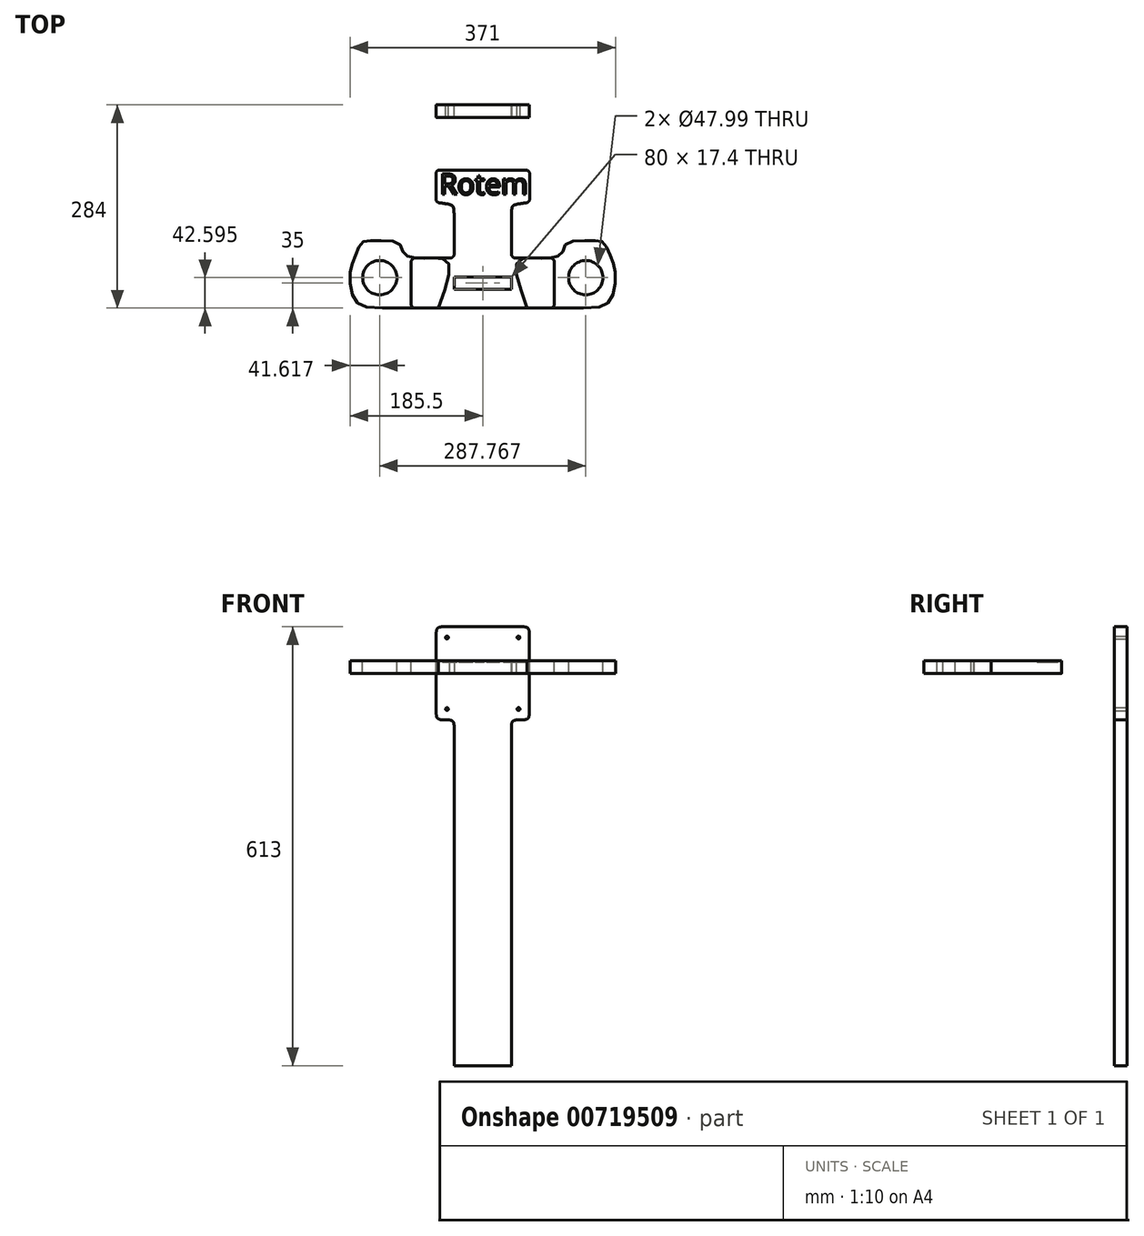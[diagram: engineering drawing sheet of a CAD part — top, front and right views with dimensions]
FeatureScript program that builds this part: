
annotation { "Feature Type Name" : "Feature", "Feature Type Description" : "" }
export const myFeature = defineFeature(function(context is Context, id is Id, definition is map)
    precondition{}
    {
        {
            var Q0;
            Q0=qCreatedBy(makeId("Front.planeOp"),FACE);
            var sketch = newSketch(context, id + "F0", { "sketchPlane" : qUnion([Q0])});
            skLineSegment(sketch, "E0.bottom", {"start": v(-65, 65) * mm, "end": v(65, 65) * mm});
            skLineSegment(sketch, "E0.top", {"start": v(-65, -65) * mm, "end": v(-40, -65) * mm});
            skLineSegment(sketch, "E0.left", {"start": v(-65, 65) * mm, "end": v(-65, -65) * mm});
            skLineSegment(sketch, "E0.right", {"start": v(65, 65) * mm, "end": v(65, -65) * mm});
            skPoint(sketch, "E0.middle", {"position": v(0, 0) * mm});
            skLineSegment(sketch, "E1", {"start": v(-65, 65) * mm, "end": v(65, -65) * mm, "construction": true});
            skLineSegment(sketch, "E2.bottom", {"start": v(-50, 50) * mm, "end": v(50, 50) * mm, "construction": true});
            skLineSegment(sketch, "E2.top", {"start": v(-50, -50) * mm, "end": v(50, -50) * mm, "construction": true});
            skLineSegment(sketch, "E2.left", {"start": v(-50, 50) * mm, "end": v(-50, -50) * mm, "construction": true});
            skLineSegment(sketch, "E2.right", {"start": v(50, 50) * mm, "end": v(50, -50) * mm, "construction": true});
            skCircle(sketch, "E3", {"center": v(-50, 50) * mm, "radius": 2 * mm});
            skCircle(sketch, "E4", {"center": v(50, 50) * mm, "radius": 2 * mm});
            skCircle(sketch, "E5", {"center": v(50, -50) * mm, "radius": 2 * mm});
            skCircle(sketch, "E6", {"center": v(-50, -50) * mm, "radius": 2 * mm});
            skLineSegment(sketch, "E7", {"start": v(-40, -548) * mm, "end": v(40, -548) * mm});
            skLineSegment(sketch, "E8", {"start": v(-40, -548) * mm, "end": v(-40, -65) * mm});
            skLineSegment(sketch, "E9", {"start": v(40, -548) * mm, "end": v(40, -65) * mm});
            skLineSegment(sketch, "E10.trimOffspring", {"start": v(40, -65) * mm, "end": v(65, -65) * mm});
            skSolve(sketch);
        }
        {
            var Q0;
            Q0=makeQuery(id+"F0.imprint","IMPRINT",FACE,{"disambiguationData":[TD([[makeQuery(id+"F0.imprint","IMPRINT",EDGE,{"derivedFrom":sQuery(id+"F0.wireOp",EDGE,"E0.bottom")}),-1.0]])]});
            var Q1;
            Q1=sQuery(id+"F0.wireOp",EDGE,"E8");
            var Q2;
            Q2=sQuery(id+"F0.wireOp",EDGE,"E0.top");
            var Q3;
            Q3=sQuery(id+"F0.wireOp",EDGE,"E0.left");
            var Q4;
            Q4=sQuery(id+"F0.wireOp",EDGE,"E0.bottom");
            var Q5;
            Q5=sQuery(id+"F0.wireOp",EDGE,"E0.right");
            var Q6;
            Q6=sQuery(id+"F0.wireOp",EDGE,"E10.trimOffspring");
            var Q7;
            Q7=sQuery(id+"F0.wireOp",EDGE,"E9");
            var Q8;
            Q8=sQuery(id+"F0.wireOp",EDGE,"E7");
            extrude(context, id + "F1", {"entities" : qUnion([Q0]), "surfaceEntities" : qUnion([Q1, Q2, Q3, Q4, Q5, Q6, Q7, Q8]), "depth" : 17.4 * mm, "offsetDistance" : 25 * mm});
        }
        {
            var Q0;
            Q0=makeQuery(id+"F1.opExtrude","SWEPT_EDGE",EDGE,{"disambiguationData":[OSD([sQuery(id+"F0.wireOp",EDGE,"E0.bottom"),sQuery(id+"F0.wireOp",EDGE,"E0.left")])]});
            var Q1;
            Q1=makeQuery(id+"F1.opExtrude","SWEPT_EDGE",EDGE,{"disambiguationData":[OSD([sQuery(id+"F0.wireOp",EDGE,"E0.bottom"),sQuery(id+"F0.wireOp",EDGE,"E0.right")])]});
            var Q2;
            Q2=makeQuery(id+"F1.opExtrude","SWEPT_EDGE",EDGE,{"disambiguationData":[OSD([sQuery(id+"F0.wireOp",EDGE,"E0.top"),sQuery(id+"F0.wireOp",EDGE,"E0.left")])]});
            var Q3;
            Q3=makeQuery(id+"F1.opExtrude","SWEPT_EDGE",EDGE,{"disambiguationData":[OSD([sQuery(id+"F0.wireOp",EDGE,"E0.top"),sQuery(id+"F0.wireOp",EDGE,"E8")])]});
            var Q4;
            Q4=makeQuery(id+"F1.opExtrude","SWEPT_EDGE",EDGE,{"disambiguationData":[OSD([sQuery(id+"F0.wireOp",EDGE,"E0.right"),sQuery(id+"F0.wireOp",EDGE,"E10.trimOffspring")])]});
            var Q5;
            Q5=makeQuery(id+"F1.opExtrude","SWEPT_EDGE",EDGE,{"disambiguationData":[OSD([sQuery(id+"F0.wireOp",EDGE,"E9"),sQuery(id+"F0.wireOp",EDGE,"E10.trimOffspring")])]});
            fillet(context, id + "F2", {"entities" : qUnion([Q0, Q1, Q2, Q3, Q4, Q5]), "radius" : 10 * mm, "tangentPropagation" : true, "rho" : 0.6, "crossSection" : FilletCrossSection.CONIC, "allowEdgeOverflow" : false});
        }
        {
            var Q0;
            Q0=qCreatedBy(makeId("Top.planeOp"),FACE);
            var sketch = newSketch(context, id + "F3", { "sketchPlane" : qUnion([Q0])});
            skLineSegment(sketch, "E11.bottom", {"start": v(-100, 35) * mm, "end": v(-40, 35) * mm});
            skLineSegment(sketch, "E11.top", {"start": v(-100, -35) * mm, "end": v(100, -35) * mm});
            skLineSegment(sketch, "E11.left", {"start": v(-100, 35) * mm, "end": v(-100, -35) * mm});
            skLineSegment(sketch, "E11.right", {"start": v(100, 35) * mm, "end": v(100, -35) * mm});
            skPoint(sketch, "E11.middle", {"position": v(0, 0) * mm});
            skPoint(sketch, "E12.middle", {"position": v(0, 35) * mm});
            skPoint(sketch, "E12.cornerSnap0", {"position": v(0, 35) * mm});
            skLineSegment(sketch, "E13.bottom", {"start": v(-40, 135) * mm, "end": v(40, 135) * mm});
            skLineSegment(sketch, "E13.left", {"start": v(-40, 135) * mm, "end": v(-40, 35) * mm});
            skLineSegment(sketch, "E13.right", {"start": v(40, 135) * mm, "end": v(40, 35) * mm});
            skPoint(sketch, "E13.top.start.orphan", {"position": v(-40, -65) * mm});
            skPoint(sketch, "E14.trimOffspring.end.orphan", {"position": v(40, -65) * mm});
            skLineSegment(sketch, "E15.trimOffspring", {"start": v(40, 35) * mm, "end": v(100, 35) * mm});
            skLineSegment(sketch, "E16.bottom", {"start": v(-40, 8.7) * mm, "end": v(40, 8.7) * mm});
            skLineSegment(sketch, "E16.top", {"start": v(-40, -8.7) * mm, "end": v(40, -8.7) * mm});
            skLineSegment(sketch, "E16.left", {"start": v(-40, 8.7) * mm, "end": v(-40, -8.7) * mm});
            skLineSegment(sketch, "E16.right", {"start": v(40, 8.7) * mm, "end": v(40, -8.7) * mm});
            skSolve(sketch);
        }
        {
            var Q0;
            Q0 = qSketchRegion(id + "F3", true);
            extrude(context, id + "F4", {"entities" : qUnion([Q0]), "depth" : 17.4 * mm, "offsetDistance" : 25 * mm});
        }
        {
            var Q0;
            Q0=makeQuery(id+"F4.opExtrude","SWEPT_BODY",BODY,{"disambiguationData":[OSD([sQuery(id+"F3.wireOp",EDGE,"E11.bottom"),sQuery(id+"F3.wireOp",EDGE,"E11.top"),sQuery(id+"F3.wireOp",EDGE,"E11.left"),sQuery(id+"F3.wireOp",EDGE,"E11.right"),sQuery(id+"F3.wireOp",EDGE,"E13.bottom"),sQuery(id+"F3.wireOp",EDGE,"E13.left"),sQuery(id+"F3.wireOp",EDGE,"E13.right"),sQuery(id+"F3.wireOp",EDGE,"E15.trimOffspring"),sQuery(id+"F3.wireOp",EDGE,"E16.bottom"),sQuery(id+"F3.wireOp",EDGE,"E16.top"),sQuery(id+"F3.wireOp",EDGE,"E16.left"),sQuery(id+"F3.wireOp",EDGE,"E16.right")])]});
            transform(context, id + "F5", {"entities" : qUnion([Q0]), "transformType" : TransformType.TRANSLATION_3D, "dx" : 0 * mm, "dy" : -249 * mm, "dz" : 0 * mm, "makeCopy" : false});
        }
        {
            var Q0;
            Q0=makeQuery(id+"F4.opExtrude","SWEPT_EDGE",EDGE,{"disambiguationData":[OSD([sQuery(id+"F3.wireOp",EDGE,"E13.right"),sQuery(id+"F3.wireOp",EDGE,"E15.trimOffspring")])]});
            var Q1;
            Q1=makeQuery(id+"F4.opExtrude","SWEPT_EDGE",EDGE,{"disambiguationData":[OSD([sQuery(id+"F3.wireOp",EDGE,"E11.right"),sQuery(id+"F3.wireOp",EDGE,"E15.trimOffspring")])]});
            var Q2;
            Q2=makeQuery(id+"F4.opExtrude","SWEPT_EDGE",EDGE,{"disambiguationData":[OSD([sQuery(id+"F3.wireOp",EDGE,"E11.top"),sQuery(id+"F3.wireOp",EDGE,"E11.right")])]});
            var Q3;
            Q3=makeQuery(id+"F4.opExtrude","SWEPT_EDGE",EDGE,{"disambiguationData":[OSD([sQuery(id+"F3.wireOp",EDGE,"E13.bottom"),sQuery(id+"F3.wireOp",EDGE,"E13.right")])]});
            var Q4;
            Q4=makeQuery(id+"F4.opExtrude","SWEPT_EDGE",EDGE,{"disambiguationData":[OSD([sQuery(id+"F3.wireOp",EDGE,"E13.bottom"),sQuery(id+"F3.wireOp",EDGE,"E13.left")])]});
            var Q5;
            Q5=makeQuery(id+"F4.opExtrude","SWEPT_EDGE",EDGE,{"disambiguationData":[OSD([sQuery(id+"F3.wireOp",EDGE,"E11.bottom"),sQuery(id+"F3.wireOp",EDGE,"E11.left")])]});
            var Q6;
            Q6=makeQuery(id+"F4.opExtrude","SWEPT_EDGE",EDGE,{"disambiguationData":[OSD([sQuery(id+"F3.wireOp",EDGE,"E11.bottom"),sQuery(id+"F3.wireOp",EDGE,"E13.left")])]});
            var Q7;
            Q7=makeQuery(id+"F4.opExtrude","SWEPT_EDGE",EDGE,{"disambiguationData":[OSD([sQuery(id+"F3.wireOp",EDGE,"E11.top"),sQuery(id+"F3.wireOp",EDGE,"E11.left")])]});
            fillet(context, id + "F6", {"entities" : qUnion([Q0, Q1, Q2, Q3, Q4, Q5, Q6, Q7]), "radius" : 5 * mm, "tangentPropagation" : true, "rho" : 0.3, "crossSection" : FilletCrossSection.CONIC, "allowEdgeOverflow" : false});
        }
        {
            var Q0;
            Q0=makeQuery(id+"F4.opExtrude","CAP_FACE",FACE,{"disambiguationData":[OSD([sQuery(id+"F3.wireOp",EDGE,"E11.bottom"),sQuery(id+"F3.wireOp",EDGE,"E11.top"),sQuery(id+"F3.wireOp",EDGE,"E11.left"),sQuery(id+"F3.wireOp",EDGE,"E11.right"),sQuery(id+"F3.wireOp",EDGE,"E13.bottom"),sQuery(id+"F3.wireOp",EDGE,"E13.left"),sQuery(id+"F3.wireOp",EDGE,"E13.right"),sQuery(id+"F3.wireOp",EDGE,"E15.trimOffspring"),sQuery(id+"F3.wireOp",EDGE,"E16.bottom"),sQuery(id+"F3.wireOp",EDGE,"E16.top"),sQuery(id+"F3.wireOp",EDGE,"E16.left"),sQuery(id+"F3.wireOp",EDGE,"E16.right")])],"isStart":false});
            var sketch = newSketch(context, id + "F7", { "sketchPlane" : qUnion([Q0])});
            skLineSegment(sketch, "E17", {"start": v(-62.08, -284) * mm, "end": v(-140.33, -284) * mm});
            skFitSpline(sketch, "E18", {"points": [v(-140.33, -284) * mm, v(-179.18, -271.37) * mm, v(-185.11, -234.14) * mm, v(-178.1, -210.94) * mm, v(-168.39, -192.05) * mm, v(-151.66, -189.9) * mm, v(-117.12, -193.67) * mm, v(-110.65, -207.16) * mm, v(-95, -214) * mm, v(-70, -214) * mm, v(-48.6, -219.57) * mm, v(-62.08, -284) * mm], "startDerivative": vector(-653.79, 6.12) * mm, "endDerivative": vector(-213.05, -582.27) * mm});
            skSolve(sketch);
        }
        {
            var Q0;
            Q0 = qSketchRegion(id + "F7", true);
            var Q1;
            Q1=makeQuery(id+"F4.opExtrude","CAP_FACE",FACE,{"disambiguationData":[OSD([sQuery(id+"F3.wireOp",EDGE,"E11.bottom"),sQuery(id+"F3.wireOp",EDGE,"E11.top"),sQuery(id+"F3.wireOp",EDGE,"E11.left"),sQuery(id+"F3.wireOp",EDGE,"E11.right"),sQuery(id+"F3.wireOp",EDGE,"E13.bottom"),sQuery(id+"F3.wireOp",EDGE,"E13.left"),sQuery(id+"F3.wireOp",EDGE,"E13.right"),sQuery(id+"F3.wireOp",EDGE,"E15.trimOffspring"),sQuery(id+"F3.wireOp",EDGE,"E16.bottom"),sQuery(id+"F3.wireOp",EDGE,"E16.top"),sQuery(id+"F3.wireOp",EDGE,"E16.left"),sQuery(id+"F3.wireOp",EDGE,"E16.right")])],"isStart":true});
            extrude(context, id + "F8", {"entities" : qUnion([Q0]), "endBound" : BoundingType.UP_TO_SURFACE, "oppositeDirection" : true, "depth" : 25 * mm, "endBoundEntityFace" : qUnion([Q1]), "offsetDistance" : 25 * mm});
        }
        {
            var Q0;
            Q0=makeQuery(id+"F8.opExtrude","SWEPT_BODY",BODY,{"disambiguationData":[OSD([sQuery(id+"F7.wireOp",EDGE,"E17"),sQuery(id+"F7.wireOp",EDGE,"E18")])]});
            var Q1;
            Q1=qCreatedBy(makeId("Right.planeOp"),FACE);
            mirror(context, id + "F9", {"entities" : qUnion([Q0]), "mirrorPlane" : qUnion([Q1])});
        }
        {
            var Q0;
            Q0=makeQuery(id+"F4.opExtrude","CAP_FACE",FACE,{"disambiguationData":[OSD([sQuery(id+"F3.wireOp",EDGE,"E11.bottom"),sQuery(id+"F3.wireOp",EDGE,"E11.top"),sQuery(id+"F3.wireOp",EDGE,"E11.left"),sQuery(id+"F3.wireOp",EDGE,"E11.right"),sQuery(id+"F3.wireOp",EDGE,"E13.bottom"),sQuery(id+"F3.wireOp",EDGE,"E13.left"),sQuery(id+"F3.wireOp",EDGE,"E13.right"),sQuery(id+"F3.wireOp",EDGE,"E15.trimOffspring"),sQuery(id+"F3.wireOp",EDGE,"E16.bottom"),sQuery(id+"F3.wireOp",EDGE,"E16.top"),sQuery(id+"F3.wireOp",EDGE,"E16.left"),sQuery(id+"F3.wireOp",EDGE,"E16.right")])],"isStart":false});
            var sketch = newSketch(context, id + "F10", { "sketchPlane" : qUnion([Q0])});
            skCircle(sketch, "E19", {"center": v(-143.88, -241.4) * mm, "radius": 24 * mm});
            skLineSegment(sketch, "E20", {"start": v(0, -114) * mm, "end": v(0, -168.08) * mm, "construction": true});
            skCircle(sketch, "E21.MirrorC", {"center": v(143.88, -241.4) * mm, "radius": 24 * mm});
            skSolve(sketch);
        }
        {
            var Q0;
            Q0 = qSketchRegion(id + "F10", true);
            extrude(context, id + "F11", {"entities" : qUnion([Q0]), "operationType" : NewBodyOperationType.REMOVE, "oppositeDirection" : true, "depth" : 25 * mm, "offsetDistance" : 25 * mm});
        }
        {
            var Q0;
            Q0=makeQuery(id+"F4.opExtrude","CAP_FACE",FACE,{"disambiguationData":[OSD([sQuery(id+"F3.wireOp",EDGE,"E11.bottom"),sQuery(id+"F3.wireOp",EDGE,"E11.top"),sQuery(id+"F3.wireOp",EDGE,"E11.left"),sQuery(id+"F3.wireOp",EDGE,"E11.right"),sQuery(id+"F3.wireOp",EDGE,"E13.bottom"),sQuery(id+"F3.wireOp",EDGE,"E13.left"),sQuery(id+"F3.wireOp",EDGE,"E13.right"),sQuery(id+"F3.wireOp",EDGE,"E15.trimOffspring"),sQuery(id+"F3.wireOp",EDGE,"E16.bottom"),sQuery(id+"F3.wireOp",EDGE,"E16.top"),sQuery(id+"F3.wireOp",EDGE,"E16.left"),sQuery(id+"F3.wireOp",EDGE,"E16.right")])],"isStart":false});
            var sketch = newSketch(context, id + "F12", { "sketchPlane" : qUnion([Q0])});
            skLineSegment(sketch, "E22.bottom", {"start": v(60.44, -136.8) * mm, "end": v(-60.44, -136.8) * mm});
            skLineSegment(sketch, "E22.top", {"start": v(60.44, -91.2) * mm, "end": v(-60.44, -91.2) * mm});
            skLineSegment(sketch, "E22.left", {"start": v(65.44, -131.8) * mm, "end": v(65.44, -96.2) * mm});
            skLineSegment(sketch, "E22.right", {"start": v(-65.44, -131.8) * mm, "end": v(-65.44, -96.2) * mm});
            skPoint(sketch, "E22.middle", {"position": v(0, -114) * mm});
            skPoint(sketch, "E23.visualSharp", {"position": v(65.44, -136.8) * mm});
            skArc(sketch, "E23.filletArc", {"start": v(60.44, -136.8) * mm, "mid": v(63.97, -135.34) * mm, "end": v(65.44, -131.8) * mm});
            skPoint(sketch, "E24.visualSharp", {"position": v(65.44, -91.2) * mm});
            skArc(sketch, "E24.filletArc", {"start": v(65.44, -96.2) * mm, "mid": v(63.97, -92.66) * mm, "end": v(60.44, -91.2) * mm});
            skPoint(sketch, "E25.visualSharp", {"position": v(-65.44, -91.2) * mm});
            skArc(sketch, "E25.filletArc", {"start": v(-60.44, -91.2) * mm, "mid": v(-63.97, -92.66) * mm, "end": v(-65.44, -96.2) * mm});
            skPoint(sketch, "E26.visualSharp", {"position": v(-65.44, -136.8) * mm});
            skArc(sketch, "E26.filletArc", {"start": v(-65.44, -131.8) * mm, "mid": v(-63.97, -135.34) * mm, "end": v(-60.44, -136.8) * mm});
            skSolve(sketch);
        }
        {
            var Q0;
            Q0 = qSketchRegion(id + "F12", true);
            var Q1;
            Q1=makeQuery(id+"F4.opExtrude","CAP_FACE",FACE,{"disambiguationData":[OSD([sQuery(id+"F3.wireOp",EDGE,"E11.bottom"),sQuery(id+"F3.wireOp",EDGE,"E11.top"),sQuery(id+"F3.wireOp",EDGE,"E11.left"),sQuery(id+"F3.wireOp",EDGE,"E11.right"),sQuery(id+"F3.wireOp",EDGE,"E13.bottom"),sQuery(id+"F3.wireOp",EDGE,"E13.left"),sQuery(id+"F3.wireOp",EDGE,"E13.right"),sQuery(id+"F3.wireOp",EDGE,"E15.trimOffspring"),sQuery(id+"F3.wireOp",EDGE,"E16.bottom"),sQuery(id+"F3.wireOp",EDGE,"E16.top"),sQuery(id+"F3.wireOp",EDGE,"E16.left"),sQuery(id+"F3.wireOp",EDGE,"E16.right")])],"isStart":true});
            extrude(context, id + "F13", {"entities" : qUnion([Q0]), "operationType" : NewBodyOperationType.ADD, "endBound" : BoundingType.UP_TO_SURFACE, "oppositeDirection" : true, "depth" : 25 * mm, "endBoundEntityFace" : qUnion([Q1]), "offsetDistance" : 25 * mm});
        }
        {
            var Q0;
            Q0=makeQuery(id+"F13.boolean.opBoolean","INTERSECT",EDGE,{"derivedFrom":[makeQuery(id+"F4.opExtrude","SWEPT_FACE",FACE,{"disambiguationData":[OSD([sQuery(id+"F3.wireOp",EDGE,"E13.right")])]}),makeQuery(id+"F13.opExtrude","SWEPT_FACE",FACE,{"disambiguationData":[OSD([sQuery(id+"F12.wireOp",EDGE,"E22.bottom")])]})]});
            var Q1;
            Q1=makeQuery(id+"F13.boolean.opBoolean","INTERSECT",EDGE,{"derivedFrom":[makeQuery(id+"F4.opExtrude","SWEPT_FACE",FACE,{"disambiguationData":[OSD([sQuery(id+"F3.wireOp",EDGE,"E13.left")])]}),makeQuery(id+"F13.opExtrude","SWEPT_FACE",FACE,{"disambiguationData":[OSD([sQuery(id+"F12.wireOp",EDGE,"E22.bottom")])]})]});
            fillet(context, id + "F14", {"entities" : qUnion([Q0, Q1]), "tangentPropagation" : true, "crossSection" : FilletCrossSection.CONIC, "radius" : 24.14 * mm, "rho" : 0.8, "defaultsChanged" : true, "vertexSettings" : [], "allowEdgeOverflow" : false});
        }
        {
            var Q0;
            Q0=makeQuery(id+"F13.boolean.opBoolean","MERGE",FACE,{"derivedFrom":[makeQuery(id+"F4.opExtrude","CAP_FACE",FACE,{"disambiguationData":[OSD([sQuery(id+"F3.wireOp",EDGE,"E11.bottom"),sQuery(id+"F3.wireOp",EDGE,"E11.top"),sQuery(id+"F3.wireOp",EDGE,"E11.left"),sQuery(id+"F3.wireOp",EDGE,"E11.right"),sQuery(id+"F3.wireOp",EDGE,"E13.bottom"),sQuery(id+"F3.wireOp",EDGE,"E13.left"),sQuery(id+"F3.wireOp",EDGE,"E13.right"),sQuery(id+"F3.wireOp",EDGE,"E15.trimOffspring"),sQuery(id+"F3.wireOp",EDGE,"E16.bottom"),sQuery(id+"F3.wireOp",EDGE,"E16.top"),sQuery(id+"F3.wireOp",EDGE,"E16.left"),sQuery(id+"F3.wireOp",EDGE,"E16.right")])],"isStart":false}),makeQuery(id+"F13.opExtrude","CAP_FACE",FACE,{"disambiguationData":[OSD([sQuery(id+"F12.wireOp",EDGE,"E22.bottom"),sQuery(id+"F12.wireOp",EDGE,"E22.top"),sQuery(id+"F12.wireOp",EDGE,"E22.left"),sQuery(id+"F12.wireOp",EDGE,"E22.right"),sQuery(id+"F12.wireOp",EDGE,"E23.filletArc"),sQuery(id+"F12.wireOp",EDGE,"E24.filletArc"),sQuery(id+"F12.wireOp",EDGE,"E25.filletArc"),sQuery(id+"F12.wireOp",EDGE,"E26.filletArc")])],"isStart":true})]});
            var sketch = newSketch(context, id + "F15", { "sketchPlane" : qUnion([Q0])});
            skText(sketch, "E27", { "text": "Rotem", "fontName": "OpenSans-Regular.ttf"});
            const initialGuessF15  = {"E27": [-0.06044, -0.12518, 1, 0, 0.02898]};
            skSetInitialGuess(sketch, initialGuessF15);
            skSolve(sketch);
        }
        {
            var Q0;
            Q0 = qSketchRegion(id + "F15", true);
            extrude(context, id + "F16", {"entities" : qUnion([Q0]), "operationType" : NewBodyOperationType.REMOVE, "oppositeDirection" : true, "depth" : 2 * mm, "offsetDistance" : 25 * mm});
        }
    });
